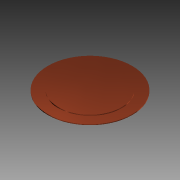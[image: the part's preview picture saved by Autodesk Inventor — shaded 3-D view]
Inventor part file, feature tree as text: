
AUTODESK INVENTOR PART (.ipt)
format: ipt  version: 2014 (Build 180170000, 170)  size: 81,408 bytes
history: native  units: in
note: dims shown in document units (in); Inventor stores cm internally (conversion verified against a paired STEP export)
features: revolve x1, sketch x1
ambient origin geometry x8: Origin, YZ Plane, XZ Plane, XY Plane, X Axis, Y Axis, Z Axis, Center Point
bodies: Solid1 (feature_tree)
feature tree (2):
  revolve  "Revolution1"  [1 undecoded]
  sketch  "Sketch1"  dims[d0=0.2362in d1=0.0039in d2=0.1772in d3=0.0047in d4=90.0deg]
note: 1 required parameter value undecoded (feature->parameter linkage not recoverable at this tier; creation-order binding heuristic only, values carry confidence <= 0.55)
